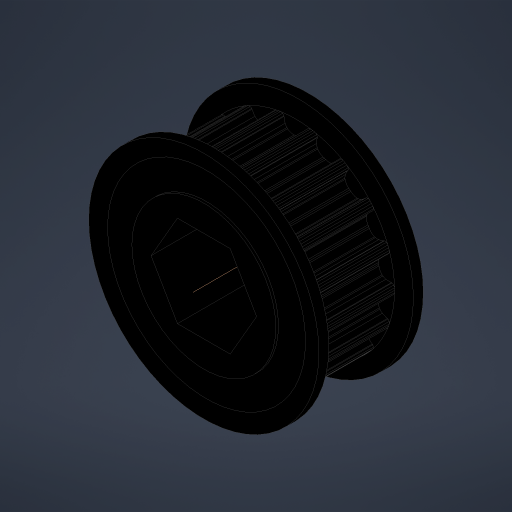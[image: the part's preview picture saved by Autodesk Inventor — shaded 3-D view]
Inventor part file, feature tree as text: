
AUTODESK INVENTOR PART (.ipt)
format: ipt  version: 2023.4 (Build 274418000, 418)  size: 647,168 bytes
history: native  units: in
note: dims shown in document units (in); Inventor stores cm internally (conversion verified against a paired STEP export)
features: plane x1, mirror x1
ambient origin geometry x8: Origin, YZ Plane, XZ Plane, XY Plane, X Axis, Y Axis, Z Axis, Center Point
bodies: Solid1 (feature_tree)
feature tree (2):
  plane  "Work Plane1"
  mirror  "Mirror1"
